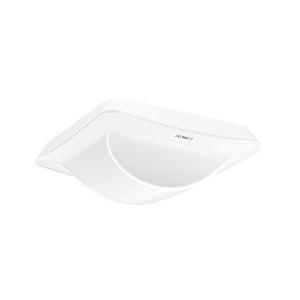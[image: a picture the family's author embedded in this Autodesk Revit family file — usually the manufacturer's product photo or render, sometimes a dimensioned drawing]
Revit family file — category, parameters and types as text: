
# Revit family: hallway_057985
name_source: partatom
category: Elektroinstallationen
revit_build: Autodesk Revit 2016 (Build: 20190508_0715(x64)
units: mm (PartAtom-declared; Revit-internal decimal feet)

## family parameters
Basisbauteil = Fläche
Beim Laden mit Abzugskörper schneiden = Nein
Bemaßung runder Anschluss = Durchmesser verwenden
Beschriftungsausrichtung beibehalten = Nein
Gemeinsam genutzt = Nein
Raumberechnungspunkt = Nein
Teiletyp = Normal

## types (1)
- Hallway
    Apparent Load = 0 VA
    Beschreibung = Type: Presence detector; Dimensions (L x W x H): 67 x 103 x 103 mm; Mains power supply: 220 – 240 V / 50 – 60 Hz; Power consumption: 1 W; Sensor Technology: High frequency; Application, place: Indoors; Application, room: Indoors, corridor / aisle; Installation site: ceiling; Installation: Concealed wiring; HF-system: 5,8 GHz; Electronic scalability: Yes; Mechanical scalability: No; Mounting height: 2 – 4 m; Optimum mounting height: 2,8 m; Detection: also through glass, wood and stud walls; Detection angle: 360 °; Angle of aperture: 140 °; Sneak-by guard: Yes; Capability of masking out individual segments: No; Reach, radial: 25 x 3 m (75 m²); Reach, tangential: 25 x 3 m (75 m²); Twilight setting TEACH: Yes; Twilight setting: 2 – 1000 lx; Time setting: 30 sec – 60 min; Switching output 1, resistive: 2000 W; Switching output 1, number of LEDs / fluorescent lamps: 8 pcs.; Switching output 1, floating: No; Constant-lighting control: No; Basic light level function: No; Functions: Group parameterisation, Semi-/fully automatic, Lighting scenario, Manual ON / ON-OFF, Neighbouring-group function, Normal / test mode; Settings via: Bluetooth; With remote control: No; Interconnection: Yes; IP-rating: IP20; Material: Plastic; Ambient temperature: -20 – 50 °C; Colour: white; Colour, RAL: 9003; Manufacturer's Warranty: 5 years; Version: COM1 - Concealed wiring; PU1, EAN: 4007841057985
    Height = 0 mm  [stored 0 ft]
    Hersteller = Steinel
    Length = 67 mm
    Maximum range = 10.579 m
    ModVariant = Nein
    Modell = 057985
    Mounting Place = Ceiling
    Mounting Type = Recessed
    Number of Poles = 1
    OnlyDefault = Ja
    Power Factor = 1
    Product Name = Hallway
    Product group = Presence detector
    ProductGroupID = 4
    Protection Class = Protection class
    Protection Degree = IP 20
    RlxData = <blob elided: 131021 chars, md5=46f73381>
    Sensor characteristics = Stretched
    Sensor type = HF
    SensorDataFile = <blob elided: 184890 chars, md5=e609621d>
    Type of entry = Motion
    Typenbild = produkt1_057985.jpg
    Typenkommentare = Product without accessories
    URL = http://relux.com
    VarID = ---
    Voltage = 0 V
    Vorgabe-Ansicht = 1800 mm
    Weight = 0.00 kg
    Width = 103 mm

note: [stored X ft] marks values corroborated as IEEE doubles in the binary element streams (Revit-internal decimal feet)

## geometry (parser evidence)
native form markers: Sweep x19
no freeform markers — native parametric forms only
